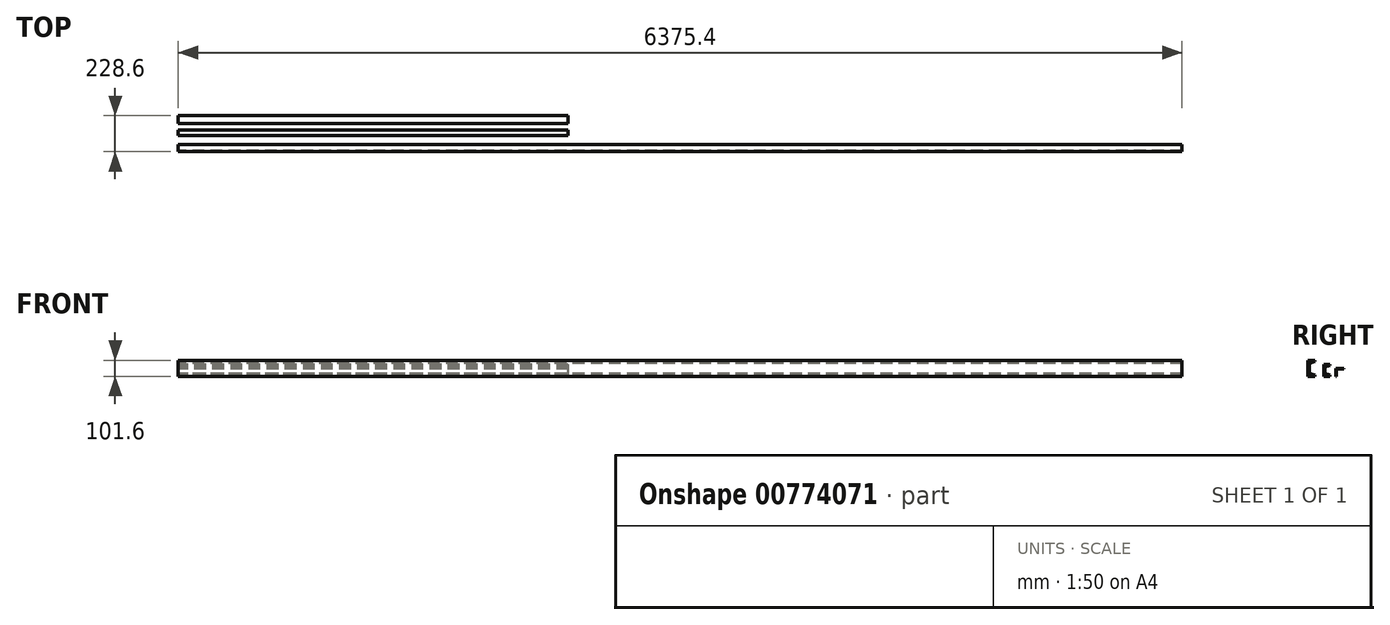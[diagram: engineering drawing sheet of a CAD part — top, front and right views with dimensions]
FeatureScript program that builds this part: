
annotation { "Feature Type Name" : "Feature", "Feature Type Description" : "" }
export const myFeature = defineFeature(function(context is Context, id is Id, definition is map)
    precondition{}
    {
        {
            var Q0;
            Q0=qCreatedBy(makeId("Right.planeOp"),FACE);
            var sketch = newSketch(context, id + "F0", { "sketchPlane" : qUnion([Q0])});
            skLineSegment(sketch, "E0", {"start": v(0, 0) * mm, "end": v(177.8, 0) * mm, "construction": true});
            skLineSegment(sketch, "E1", {"start": v(0, 0) * mm, "end": v(0, 101.6) * mm});
            skLineSegment(sketch, "E2", {"start": v(0, 101.6) * mm, "end": v(43.69, 101.6) * mm});
            skLineSegment(sketch, "E3", {"start": v(43.69, 101.6) * mm, "end": v(43.69, 94.08) * mm});
            skLineSegment(sketch, "E4", {"start": v(43.69, 94.08) * mm, "end": v(8.15, 82.55) * mm});
            skLineSegment(sketch, "E5", {"start": v(8.15, 82.55) * mm, "end": v(8.15, 19.05) * mm});
            skLineSegment(sketch, "E6", {"start": v(8.15, 19.05) * mm, "end": v(43.69, 7.52) * mm});
            skLineSegment(sketch, "E7", {"start": v(43.69, 7.52) * mm, "end": v(43.69, 0) * mm});
            skLineSegment(sketch, "E8", {"start": v(43.69, 0) * mm, "end": v(0, 0) * mm});
            skLineSegment(sketch, "E9", {"start": v(101.6, 0) * mm, "end": v(101.6, 76.2) * mm});
            skLineSegment(sketch, "E10", {"start": v(101.6, 76.2) * mm, "end": v(137.41, 76.2) * mm});
            skLineSegment(sketch, "E11", {"start": v(137.41, 76.2) * mm, "end": v(137.41, 69.27) * mm});
            skLineSegment(sketch, "E12", {"start": v(137.41, 69.27) * mm, "end": v(105.92, 58.74) * mm});
            skLineSegment(sketch, "E13", {"start": v(105.92, 58.74) * mm, "end": v(105.92, 17.46) * mm});
            skLineSegment(sketch, "E14", {"start": v(105.92, 17.46) * mm, "end": v(137.41, 6.93) * mm});
            skLineSegment(sketch, "E15", {"start": v(137.41, 6.93) * mm, "end": v(137.41, 0) * mm});
            skLineSegment(sketch, "E16", {"start": v(137.41, 0) * mm, "end": v(101.6, 0) * mm});
            skLineSegment(sketch, "E17", {"start": v(177.8, 0) * mm, "end": v(177.8, 50.8) * mm});
            skLineSegment(sketch, "E18", {"start": v(177.8, 50.8) * mm, "end": v(228.6, 50.8) * mm});
            skLineSegment(sketch, "E19", {"start": v(228.6, 50.8) * mm, "end": v(228.6, 47.63) * mm});
            skLineSegment(sketch, "E20", {"start": v(228.6, 47.63) * mm, "end": v(180.97, 47.63) * mm});
            skLineSegment(sketch, "E21", {"start": v(180.97, 47.63) * mm, "end": v(180.97, 0) * mm});
            skLineSegment(sketch, "E22", {"start": v(180.97, 0) * mm, "end": v(177.8, 0) * mm});
            skSolve(sketch);
        }
        {
            var Q0;
            Q0=makeQuery(id+"F0.imprint","IMPRINT",FACE,{"disambiguationData":[TD([[makeQuery(id+"F0.imprint","IMPRINT",EDGE,{"derivedFrom":sQuery(id+"F0.wireOp",EDGE,"E1")}),-1.0]])]});
            extrude(context, id + "F1", {"entities" : qUnion([Q0]), "depth" : 6375.4 * mm, "offsetDistance" : 25.4 * mm});
        }
        {
            var Q0;
            Q0=makeQuery(id+"F0.imprint","IMPRINT",FACE,{"disambiguationData":[TD([[makeQuery(id+"F0.imprint","IMPRINT",EDGE,{"derivedFrom":sQuery(id+"F0.wireOp",EDGE,"E9")}),-1.0]])]});
            extrude(context, id + "F2", {"entities" : qUnion([Q0]), "depth" : 2476.5 * mm, "offsetDistance" : 25.4 * mm});
        }
        {
            var Q0;
            Q0=makeQuery(id+"F0.imprint","IMPRINT",FACE,{"disambiguationData":[TD([[makeQuery(id+"F0.imprint","IMPRINT",EDGE,{"derivedFrom":sQuery(id+"F0.wireOp",EDGE,"E17")}),-1.0]])]});
            extrude(context, id + "F3", {"entities" : qUnion([Q0]), "depth" : 2476.5 * mm, "offsetDistance" : 25.4 * mm});
        }
    });
